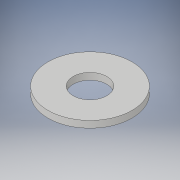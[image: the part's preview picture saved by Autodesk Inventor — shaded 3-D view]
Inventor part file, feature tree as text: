
AUTODESK INVENTOR PART (.ipt)
format: ipt  version: 2019 (Build 230136000, 136)  size: 96,256 bytes
history: native  units: in
note: dims shown in document units (in); Inventor stores cm internally (conversion verified against a paired STEP export)
features: extrude x1, sketch x1
ambient origin geometry x8: Origin, YZ Plane, XZ Plane, XY Plane, X Axis, Y Axis, Z Axis, Center Point
bodies: Solid1 (feature_tree)
feature tree (2):
  extrude  "Extrusion1"  Depth=0.06in
  sketch  "Sketch1"  dims[d0=0.3in d1=0.75in d2=0.06in d3=0.0in]
